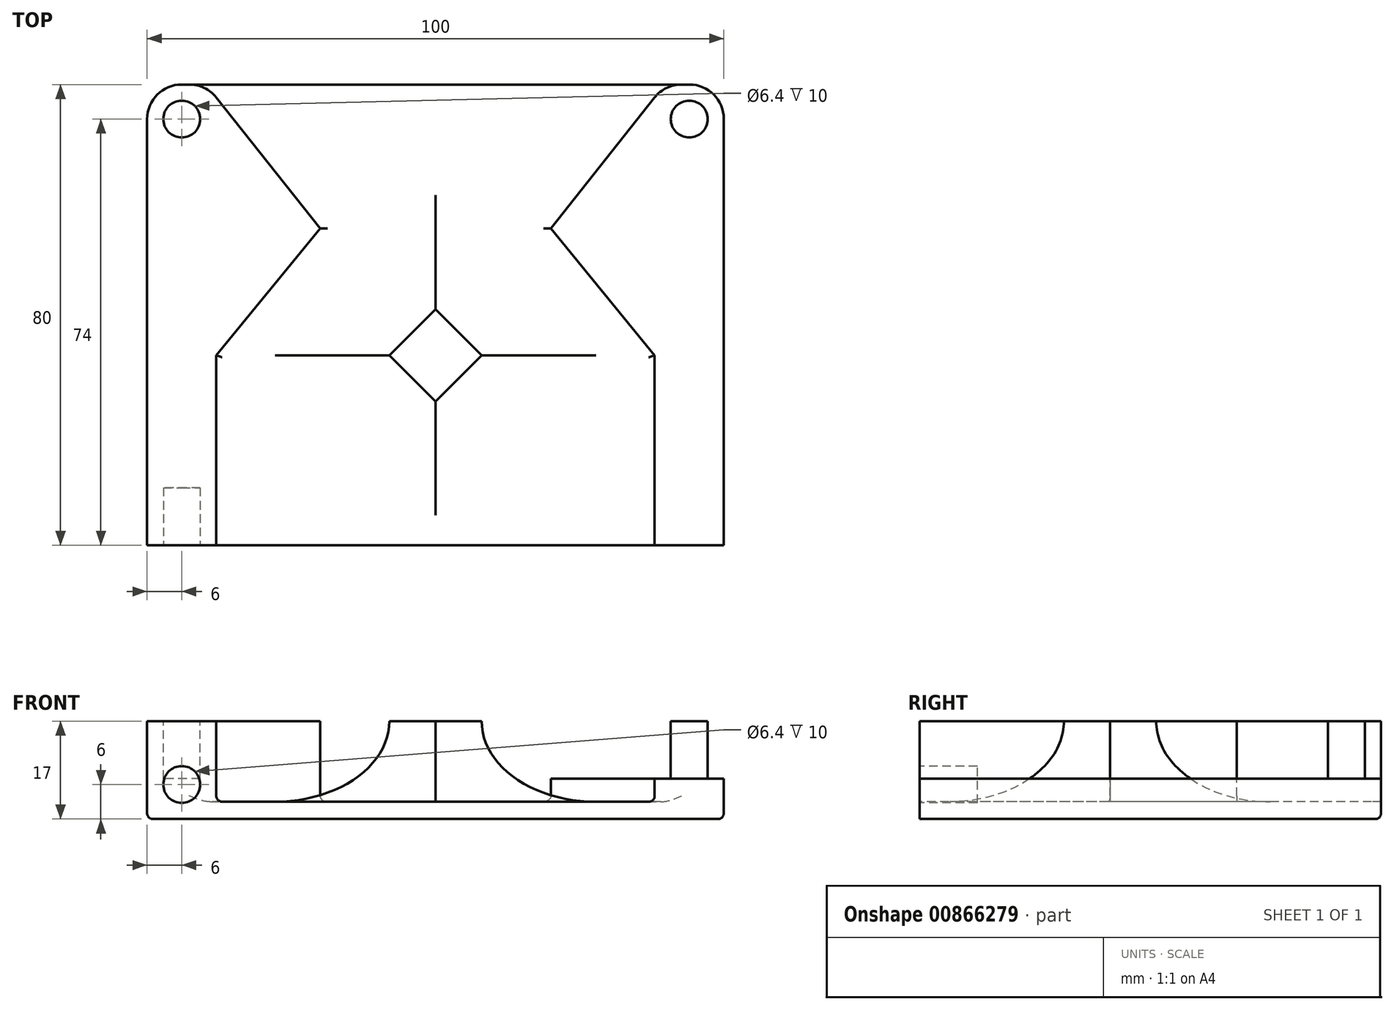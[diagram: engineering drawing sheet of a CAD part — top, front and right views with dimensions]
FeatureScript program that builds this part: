
annotation { "Feature Type Name" : "Feature", "Feature Type Description" : "" }
export const myFeature = defineFeature(function(context is Context, id is Id, definition is map)
    precondition{}
    {
        {
            var Q0;
            Q0=qCreatedBy(makeId("Top.planeOp"),FACE);
            var sketch = newSketch(context, id + "F0", { "sketchPlane" : qUnion([Q0])});
            skLineSegment(sketch, "E0.bottom", {"start": v(0, 0) * mm, "end": v(50, 0) * mm});
            skLineSegment(sketch, "E0.top", {"start": v(6, 80) * mm, "end": v(50, 80) * mm});
            skLineSegment(sketch, "E0.left", {"start": v(0, 0) * mm, "end": v(0, 74) * mm});
            skLineSegment(sketch, "E0.right", {"start": v(50, 0) * mm, "end": v(50, 80) * mm, "construction": true});
            skLineSegment(sketch, "E1.MirrorCS", {"start": v(94, 80) * mm, "end": v(50, 80) * mm});
            skLineSegment(sketch, "E2.MirrorCS", {"start": v(100, 0) * mm, "end": v(100, 74) * mm});
            skLineSegment(sketch, "E3.MirrorCS", {"start": v(100, 0) * mm, "end": v(50, 0) * mm});
            skPoint(sketch, "E4.visualSharp", {"position": v(0, 80) * mm});
            skArc(sketch, "E4.filletArc", {"start": v(6, 80) * mm, "mid": v(1.76, 78.24) * mm, "end": v(0, 74) * mm});
            skPoint(sketch, "E5.visualSharp", {"position": v(100, 80) * mm});
            skArc(sketch, "E5.filletArc", {"start": v(100, 74) * mm, "mid": v(98.24, 78.24) * mm, "end": v(94, 80) * mm});
            skSolve(sketch);
        }
        {
            var Q0;
            Q0=qCreatedBy(makeId("Top.planeOp"),FACE);
            cPlane(context, id + "F1", {"entities" : qUnion([Q0]), "cplaneType" : CPlaneType.OFFSET, "offset" : 17 * mm, "width" : 150 * mm, "height" : 150 * mm});
        }
        {
            var Q0;
            Q0=qCreatedBy(id+"F1.planeOp",FACE);
            var sketch = newSketch(context, id + "F2", { "sketchPlane" : qUnion([Q0])});
            skLineSegment(sketch, "E6.bottom", {"start": v(0, 0) * mm, "end": v(50, 0) * mm});
            skLineSegment(sketch, "E6.top", {"start": v(6, 80) * mm, "end": v(7.3, 80) * mm});
            skLineSegment(sketch, "E6.left", {"start": v(0, 0) * mm, "end": v(0, 74) * mm});
            skLineSegment(sketch, "E6.right", {"start": v(50, 0) * mm, "end": v(50, 80) * mm, "construction": true});
            skCircle(sketch, "E7", {"center": v(6, 74) * mm, "radius": 3.2 * mm});
            skPoint(sketch, "E8.visualSharp", {"position": v(0, 80) * mm});
            skArc(sketch, "E8.filletArc", {"start": v(6, 80) * mm, "mid": v(1.76, 78.24) * mm, "end": v(0, 74) * mm});
            skArc(sketch, "E9.filletArc", {"start": v(12, 77.74) * mm, "mid": v(9.91, 79.4) * mm, "end": v(7.3, 80) * mm});
            skLineSegment(sketch, "E10", {"start": v(50, 41) * mm, "end": v(42, 33) * mm});
            skLineSegment(sketch, "E11", {"start": v(42, 33) * mm, "end": v(50, 25) * mm});
            skLineSegment(sketch, "E12", {"start": v(12, 77.74) * mm, "end": v(30, 55) * mm});
            skLineSegment(sketch, "E13", {"start": v(30, 55) * mm, "end": v(12, 33) * mm});
            skLineSegment(sketch, "E14", {"start": v(12, 33) * mm, "end": v(12, 0) * mm});
            skLineSegment(sketch, "E15.MirrorCS", {"start": v(94, 80) * mm, "end": v(92.7, 80) * mm});
            skArc(sketch, "E16.MirrorCS", {"start": v(88, 77.74) * mm, "mid": v(90.09, 79.4) * mm, "end": v(92.7, 80) * mm});
            skArc(sketch, "E17.MirrorCS", {"start": v(94, 80) * mm, "mid": v(98.24, 78.24) * mm, "end": v(100, 74) * mm});
            skCircle(sketch, "E18.MirrorC", {"center": v(94, 74) * mm, "radius": 3.2 * mm});
            skPoint(sketch, "E19.MirrorP", {"position": v(100, 80) * mm});
            skLineSegment(sketch, "E20.MirrorCS", {"start": v(100, 0) * mm, "end": v(100, 74) * mm});
            skLineSegment(sketch, "E21.MirrorCS", {"start": v(50, 41) * mm, "end": v(58, 33) * mm});
            skLineSegment(sketch, "E22.MirrorCS", {"start": v(100, 0) * mm, "end": v(50, 0) * mm});
            skLineSegment(sketch, "E23.MirrorCS", {"start": v(88, 77.74) * mm, "end": v(70, 55) * mm});
            skLineSegment(sketch, "E24.MirrorCS", {"start": v(58, 33) * mm, "end": v(50, 25) * mm});
            skLineSegment(sketch, "E25.MirrorCS", {"start": v(70, 55) * mm, "end": v(88, 33) * mm});
            skLineSegment(sketch, "E26.MirrorCS", {"start": v(88, 33) * mm, "end": v(88, 0) * mm});
            skLineSegment(sketch, "E27", {"start": v(6, 80) * mm, "end": v(94, 80) * mm});
            skSolve(sketch);
        }
        {
            var Q0;
            Q0=makeQuery(id+"F0.imprint","IMPRINT",FACE,{"disambiguationData":[TD([[makeQuery(id+"F0.imprint","IMPRINT",EDGE,{"derivedFrom":sQuery(id+"F0.wireOp",EDGE,"E0.bottom")}),1.0]])]});
            extrude(context, id + "F3", {"entities" : qUnion([Q0]), "depth" : 17 * mm, "offsetDistance" : 25 * mm});
        }
        {
            var Q0;
            Q0=qCreatedBy(makeId("Front.planeOp"),FACE);
            var sketch = newSketch(context, id + "F4", { "sketchPlane" : qUnion([Q0])});
            skLineSegment(sketch, "E28", {"start": v(50, 39.45) * mm, "end": v(50, -14.22) * mm, "construction": true});
            skCircle(sketch, "E29", {"center": v(6, 6) * mm, "radius": 3.2 * mm});
            skCircle(sketch, "E30.MirrorC", {"center": v(94, 6) * mm, "radius": 3.2 * mm});
            skSolve(sketch);
        }
        {
            var Q0;
            {var subQ6=sQuery(id+"F2.wireOp",EDGE,"E9.filletArc");Q0=makeQuery(id+"F2.imprint","IMPRINT",FACE,{"disambiguationData":[TD([[makeQuery(id+"F2.imprint","IMPRINT",EDGE,{"derivedFrom":subQ6}),-1.0]])]});}
            extrude(context, id + "F5", {"entities" : qUnion([Q0]), "operationType" : NewBodyOperationType.REMOVE, "oppositeDirection" : true, "depth" : 14 * mm, "offsetDistance" : 25 * mm});
        }
        {
            var Q0;
            Q0=makeQuery(id+"F2.imprint","IMPRINT",FACE,{"disambiguationData":[TD([[makeQuery(id+"F2.imprint","IMPRINT",EDGE,{"derivedFrom":sQuery(id+"F2.wireOp",EDGE,"E7")}),1.0]])]});
            var Q1;
            Q1=makeQuery(id+"F2.imprint","IMPRINT",FACE,{"disambiguationData":[TD([[makeQuery(id+"F2.imprint","IMPRINT",EDGE,{"derivedFrom":sQuery(id+"F2.wireOp",EDGE,"E18.MirrorC")}),-1.0]])]});
            extrude(context, id + "F6", {"entities" : qUnion([Q0, Q1]), "operationType" : NewBodyOperationType.REMOVE, "oppositeDirection" : true, "depth" : 10 * mm, "offsetDistance" : 25 * mm});
        }
        {
            var Q0;
            Q0=makeQuery(id+"F4.imprint","IMPRINT",FACE,{"disambiguationData":[TD([[makeQuery(id+"F4.imprint","IMPRINT",EDGE,{"derivedFrom":sQuery(id+"F4.wireOp",EDGE,"E29")}),1.0]])]});
            var Q1;
            Q1=makeQuery(id+"F4.imprint","IMPRINT",FACE,{"disambiguationData":[TD([[makeQuery(id+"F4.imprint","IMPRINT",EDGE,{"derivedFrom":sQuery(id+"F4.wireOp",EDGE,"E30.MirrorC")}),-1.0]])]});
            extrude(context, id + "F7", {"entities" : qUnion([Q0, Q1]), "operationType" : NewBodyOperationType.REMOVE, "oppositeDirection" : true, "depth" : 10 * mm, "offsetDistance" : 25 * mm});
        }
        {
            var Q0;
            Q0=makeQuery(id+"F5.boolean.opBoolean","COPY",EDGE,{"derivedFrom":makeQuery(id+"F5.opExtrude","CAP_EDGE",EDGE,{"disambiguationData":[OSD([sQuery(id+"F2.wireOp",EDGE,"E13")])],"isStart":false})});
            var Q1;
            Q1=makeQuery(id+"F5.boolean.opBoolean","COPY",EDGE,{"derivedFrom":makeQuery(id+"F5.opExtrude","CAP_EDGE",EDGE,{"disambiguationData":[OSD([sQuery(id+"F2.wireOp",EDGE,"E14")])],"isStart":false})});
            var Q2;
            Q2=makeQuery(id+"F5.boolean.opBoolean","COPY",EDGE,{"derivedFrom":makeQuery(id+"F5.opExtrude","CAP_EDGE",EDGE,{"disambiguationData":[OSD([sQuery(id+"F2.wireOp",EDGE,"E12")])],"isStart":false})});
            var Q3;
            Q3=makeQuery(id+"F5.boolean.opBoolean","COPY",EDGE,{"derivedFrom":makeQuery(id+"F5.opExtrude","CAP_EDGE",EDGE,{"disambiguationData":[OSD([sQuery(id+"F2.wireOp",EDGE,"E23.MirrorCS")])],"isStart":false})});
            var Q4;
            Q4=makeQuery(id+"F5.boolean.opBoolean","COPY",EDGE,{"derivedFrom":makeQuery(id+"F5.opExtrude","CAP_EDGE",EDGE,{"disambiguationData":[OSD([sQuery(id+"F2.wireOp",EDGE,"E25.MirrorCS")])],"isStart":false})});
            var Q5;
            Q5=makeQuery(id+"F5.boolean.opBoolean","COPY",EDGE,{"derivedFrom":makeQuery(id+"F5.opExtrude","CAP_EDGE",EDGE,{"disambiguationData":[OSD([sQuery(id+"F2.wireOp",EDGE,"E26.MirrorCS")])],"isStart":false})});
            var Q6;
            Q6=makeQuery(id+"F3.opExtrude","CAP_EDGE",EDGE,{"disambiguationData":[OSD([sQuery(id+"F0.wireOp",EDGE,"E0.top"),sQuery(id+"F0.wireOp",EDGE,"E1.MirrorCS")])],"isStart":true});
            var Q7;
            Q7=makeQuery(id+"F6.boolean.opBoolean","COPY",EDGE,{"derivedFrom":makeQuery(id+"F6.opExtrude","CAP_EDGE",EDGE,{"disambiguationData":[OSD([sQuery(id+"F2.wireOp",EDGE,"E7")])],"isStart":true})});
            var Q8;
            Q8=makeQuery(id+"F6.boolean.opBoolean","COPY",EDGE,{"derivedFrom":makeQuery(id+"F6.opExtrude","CAP_EDGE",EDGE,{"disambiguationData":[OSD([sQuery(id+"F2.wireOp",EDGE,"E18.MirrorC")])],"isStart":true})});
            var Q9;
            Q9=makeQuery(id+"F7.boolean.opBoolean","COPY",EDGE,{"derivedFrom":makeQuery(id+"F7.opExtrude","CAP_EDGE",EDGE,{"disambiguationData":[OSD([sQuery(id+"F4.wireOp",EDGE,"E30.MirrorC")])],"isStart":true})});
            var Q10;
            Q10=makeQuery(id+"F7.boolean.opBoolean","COPY",EDGE,{"derivedFrom":makeQuery(id+"F7.opExtrude","CAP_EDGE",EDGE,{"disambiguationData":[OSD([sQuery(id+"F4.wireOp",EDGE,"E29")])],"isStart":true})});
            var Q11;
            Q11=makeQuery(id+"F5.boolean.opBoolean","COPY",EDGE,{"derivedFrom":makeQuery(id+"F5.opExtrude","CAP_EDGE",EDGE,{"disambiguationData":[OSD([sQuery(id+"F2.wireOp",EDGE,"E27")])],"isStart":false})});
            fillet(context, id + "F8", {"entities" : qUnion([Q0, Q1, Q2, Q3, Q4, Q5, Q6, Q7, Q8, Q9, Q10, Q11]), "radius" : 1 * mm, "tangentPropagation" : true, "allowEdgeOverflow" : false});
        }
        {
            var Q0;
            Q0=makeQuery(id+"F5.boolean.opBoolean","COPY",EDGE,{"derivedFrom":makeQuery(id+"F5.opExtrude","CAP_EDGE",EDGE,{"disambiguationData":[OSD([sQuery(id+"F2.wireOp",EDGE,"E24.MirrorCS")])],"isStart":false})});
            var Q1;
            Q1=makeQuery(id+"F5.boolean.opBoolean","COPY",EDGE,{"derivedFrom":makeQuery(id+"F5.opExtrude","CAP_EDGE",EDGE,{"disambiguationData":[OSD([sQuery(id+"F2.wireOp",EDGE,"E11")])],"isStart":false})});
            var Q2;
            Q2=makeQuery(id+"F5.boolean.opBoolean","COPY",EDGE,{"derivedFrom":makeQuery(id+"F5.opExtrude","CAP_EDGE",EDGE,{"disambiguationData":[OSD([sQuery(id+"F2.wireOp",EDGE,"E21.MirrorCS")])],"isStart":false})});
            var Q3;
            Q3=makeQuery(id+"F5.boolean.opBoolean","COPY",EDGE,{"derivedFrom":makeQuery(id+"F5.opExtrude","CAP_EDGE",EDGE,{"disambiguationData":[OSD([sQuery(id+"F2.wireOp",EDGE,"E10")])],"isStart":false})});
            fillet(context, id + "F9", {"entities" : qUnion([Q0, Q1, Q2, Q3]), "radius" : 14 * mm, "tangentPropagation" : true, "allowEdgeOverflow" : false});
        }
    });
